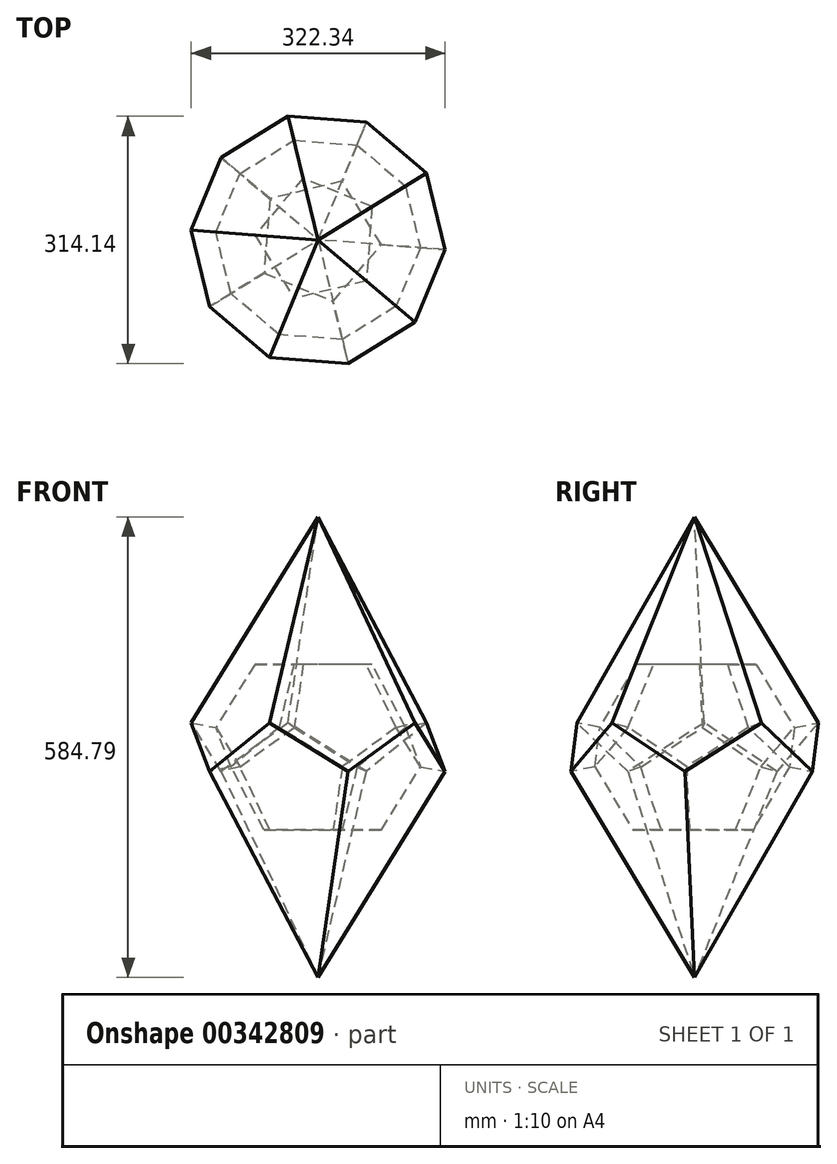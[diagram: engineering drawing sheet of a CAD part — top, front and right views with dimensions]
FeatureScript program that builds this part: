
annotation { "Feature Type Name" : "Feature", "Feature Type Description" : "" }
export const myFeature = defineFeature(function(context is Context, id is Id, definition is map)
    precondition{}
    {
        {
            var Q0;
            Q0=qCreatedBy(makeId("Top.planeOp"),FACE);
            var sketch = newSketch(context, id + "F0", { "sketchPlane" : qUnion([Q0])});
            skCircle(sketch, "E0.cCircle", {"center": v(0, 0) * mm, "radius": 80.82 * mm, "construction": true});
            skLineSegment(sketch, "E0.0", {"start": v(99.6, -7.58) * mm, "end": v(23.57, -97.07) * mm});
            skLineSegment(sketch, "E0.1", {"start": v(23.57, -97.07) * mm, "end": v(-85.04, -52.42) * mm});
            skLineSegment(sketch, "E0.2", {"start": v(-85.04, -52.42) * mm, "end": v(-76.13, 64.68) * mm});
            skLineSegment(sketch, "E0.3", {"start": v(-76.13, 64.68) * mm, "end": v(37.99, 92.39) * mm});
            skLineSegment(sketch, "E0.4", {"start": v(37.99, 92.39) * mm, "end": v(99.6, -7.58) * mm});
            skPoint(sketch, "E0.0.midPoint", {"position": v(61.59, -52.33) * mm});
            skSolve(sketch);
        }
        {
            var Q0;
            Q0=makeQuery(id+"F0.imprint","IMPRINT",FACE,{"disambiguationData":[TD([[makeQuery(id+"F0.imprint","IMPRINT",EDGE,{"derivedFrom":sQuery(id+"F0.wireOp",EDGE,"E0.0")}),-1.0]])]});
            extrude(context, id + "F1", {"entities" : qUnion([Q0]), "depth" : 25.4 * mm});
        }
        {
            var Q0;
            Q0=makeQuery(id+"F1.opExtrude","CAP_EDGE",EDGE,{"disambiguationData":[OSD([sQuery(id+"F0.wireOp",EDGE,"E0.1")])],"isStart":false});
            var Q1;
            Q1=makeQuery(id+"F1.opExtrude","CAP_EDGE",EDGE,{"disambiguationData":[OSD([sQuery(id+"F0.wireOp",EDGE,"E0.2")])],"isStart":false});
            var Q2;
            Q2=makeQuery(id+"F1.opExtrude","CAP_EDGE",EDGE,{"disambiguationData":[OSD([sQuery(id+"F0.wireOp",EDGE,"E0.3")])],"isStart":false});
            var Q3;
            Q3=makeQuery(id+"F1.opExtrude","CAP_EDGE",EDGE,{"disambiguationData":[OSD([sQuery(id+"F0.wireOp",EDGE,"E0.4")])],"isStart":false});
            var Q4;
            Q4=makeQuery(id+"F1.opExtrude","CAP_EDGE",EDGE,{"disambiguationData":[OSD([sQuery(id+"F0.wireOp",EDGE,"E0.0")])],"isStart":false});
            chamfer(context, id + "F2", {"entities" : qUnion([Q0, Q1, Q2, Q3, Q4]), "chamferType" : ChamferType.OFFSET_ANGLE, "width" : 25.4 * mm, "oppositeDirection" : false, "angle" : 31.72 * degree, "tangentPropagation" : true});
        }
        {
            var Q0;
            Q0=makeQuery(id+"F1.opExtrude","SWEPT_BODY",BODY,{"disambiguationData":[OSD([sQuery(id+"F0.wireOp",EDGE,"E0.0"),sQuery(id+"F0.wireOp",EDGE,"E0.1"),sQuery(id+"F0.wireOp",EDGE,"E0.2"),sQuery(id+"F0.wireOp",EDGE,"E0.3"),sQuery(id+"F0.wireOp",EDGE,"E0.4")])]});
            var Q1;
            Q1=makeQuery(id+"F2.opChamfer","BLEND_EDGE",EDGE,{"blendedFrom":[makeQuery(id+"F1.opExtrude","CAP_EDGE",EDGE,{"disambiguationData":[OSD([sQuery(id+"F0.wireOp",EDGE,"E0.1")])],"isStart":false}),makeQuery(id+"F1.opExtrude","CAP_EDGE",EDGE,{"disambiguationData":[OSD([sQuery(id+"F0.wireOp",EDGE,"E0.2")])],"isStart":false})],"blendedInto":[]});
            circularPattern(context, id + "F3", {"entities" : qUnion([Q0]), "axis" : qUnion([Q1]), "angle" : 360 * degree, "instanceCount" : 3, "equalSpace" : true});
        }
        {
            var Q0;
            Q0=makeQuery(id+"F1.opExtrude","SWEPT_BODY",BODY,{"disambiguationData":[OSD([sQuery(id+"F0.wireOp",EDGE,"E0.0"),sQuery(id+"F0.wireOp",EDGE,"E0.1"),sQuery(id+"F0.wireOp",EDGE,"E0.2"),sQuery(id+"F0.wireOp",EDGE,"E0.3"),sQuery(id+"F0.wireOp",EDGE,"E0.4")])]});
            var Q1;
            Q1=makeQuery(id+"F3.opPattern","COPY",BODY,{"derivedFrom":makeQuery(id+"F1.opExtrude","SWEPT_BODY",BODY,{"disambiguationData":[OSD([sQuery(id+"F0.wireOp",EDGE,"E0.0"),sQuery(id+"F0.wireOp",EDGE,"E0.1"),sQuery(id+"F0.wireOp",EDGE,"E0.2"),sQuery(id+"F0.wireOp",EDGE,"E0.3"),sQuery(id+"F0.wireOp",EDGE,"E0.4")])]}),"instanceName":"1"});
            var Q2;
            Q2=makeQuery(id+"F3.opPattern","COPY",BODY,{"derivedFrom":makeQuery(id+"F1.opExtrude","SWEPT_BODY",BODY,{"disambiguationData":[OSD([sQuery(id+"F0.wireOp",EDGE,"E0.0"),sQuery(id+"F0.wireOp",EDGE,"E0.1"),sQuery(id+"F0.wireOp",EDGE,"E0.2"),sQuery(id+"F0.wireOp",EDGE,"E0.3"),sQuery(id+"F0.wireOp",EDGE,"E0.4")])]}),"instanceName":"2"});
            var Q3;
            Q3=makeQuery(id+"F2.opChamfer","BLEND_EDGE",EDGE,{"blendedFrom":[makeQuery(id+"F1.opExtrude","CAP_EDGE",EDGE,{"disambiguationData":[OSD([sQuery(id+"F0.wireOp",EDGE,"E0.0")])],"isStart":false}),makeQuery(id+"F1.opExtrude","CAP_EDGE",EDGE,{"disambiguationData":[OSD([sQuery(id+"F0.wireOp",EDGE,"E0.4")])],"isStart":false})],"blendedInto":[]});
            transform(context, id + "F4", {"entities" : qUnion([Q0, Q1, Q2]), "transformType" : TransformType.ROTATION, "transformAxis" : qUnion([Q3]), "angle" : 120 * degree, "makeCopy" : true});
        }
        {
            var Q0;
            Q0=makeQuery(id+"F4.opPattern","COPY",BODY,{"derivedFrom":makeQuery(id+"F3.opPattern","COPY",BODY,{"derivedFrom":makeQuery(id+"F1.opExtrude","SWEPT_BODY",BODY,{"disambiguationData":[OSD([sQuery(id+"F0.wireOp",EDGE,"E0.0"),sQuery(id+"F0.wireOp",EDGE,"E0.1"),sQuery(id+"F0.wireOp",EDGE,"E0.2"),sQuery(id+"F0.wireOp",EDGE,"E0.3"),sQuery(id+"F0.wireOp",EDGE,"E0.4")])]}),"instanceName":"1"}),"instanceName":"1"});
            var Q1;
            Q1=makeQuery(id+"F4.opPattern","COPY",BODY,{"derivedFrom":makeQuery(id+"F3.opPattern","COPY",BODY,{"derivedFrom":makeQuery(id+"F1.opExtrude","SWEPT_BODY",BODY,{"disambiguationData":[OSD([sQuery(id+"F0.wireOp",EDGE,"E0.0"),sQuery(id+"F0.wireOp",EDGE,"E0.1"),sQuery(id+"F0.wireOp",EDGE,"E0.2"),sQuery(id+"F0.wireOp",EDGE,"E0.3"),sQuery(id+"F0.wireOp",EDGE,"E0.4")])]}),"instanceName":"2"}),"instanceName":"1"});
            var Q2;
            Q2=makeQuery(id+"F4.opPattern","COPY",BODY,{"derivedFrom":makeQuery(id+"F1.opExtrude","SWEPT_BODY",BODY,{"disambiguationData":[OSD([sQuery(id+"F0.wireOp",EDGE,"E0.0"),sQuery(id+"F0.wireOp",EDGE,"E0.1"),sQuery(id+"F0.wireOp",EDGE,"E0.2"),sQuery(id+"F0.wireOp",EDGE,"E0.3"),sQuery(id+"F0.wireOp",EDGE,"E0.4")])]}),"instanceName":"1"});
            var Q3;
            Q3=makeQuery(id+"F4.opPattern","COPY",EDGE,{"derivedFrom":makeQuery(id+"F3.opPattern","COPY",EDGE,{"derivedFrom":makeQuery(id+"F2.opChamfer","BLEND_EDGE",EDGE,{"blendedFrom":[makeQuery(id+"F1.opExtrude","CAP_EDGE",EDGE,{"disambiguationData":[OSD([sQuery(id+"F0.wireOp",EDGE,"E0.0")])],"isStart":false}),makeQuery(id+"F1.opExtrude","CAP_EDGE",EDGE,{"disambiguationData":[OSD([sQuery(id+"F0.wireOp",EDGE,"E0.4")])],"isStart":false})],"blendedInto":[]}),"instanceName":"2"}),"instanceName":"1"});
            transform(context, id + "F5", {"entities" : qUnion([Q0, Q1, Q2]), "transformType" : TransformType.ROTATION, "transformAxis" : qUnion([Q3]), "angle" : 120 * degree, "makeCopy" : true});
        }
        {
            var Q0;
            Q0=makeQuery(id+"F5.opPattern","COPY",BODY,{"derivedFrom":makeQuery(id+"F4.opPattern","COPY",BODY,{"derivedFrom":makeQuery(id+"F1.opExtrude","SWEPT_BODY",BODY,{"disambiguationData":[OSD([sQuery(id+"F0.wireOp",EDGE,"E0.0"),sQuery(id+"F0.wireOp",EDGE,"E0.1"),sQuery(id+"F0.wireOp",EDGE,"E0.2"),sQuery(id+"F0.wireOp",EDGE,"E0.3"),sQuery(id+"F0.wireOp",EDGE,"E0.4")])]}),"instanceName":"1"}),"instanceName":"1"});
            var Q1;
            Q1=makeQuery(id+"F4.opPattern","COPY",BODY,{"derivedFrom":makeQuery(id+"F3.opPattern","COPY",BODY,{"derivedFrom":makeQuery(id+"F1.opExtrude","SWEPT_BODY",BODY,{"disambiguationData":[OSD([sQuery(id+"F0.wireOp",EDGE,"E0.0"),sQuery(id+"F0.wireOp",EDGE,"E0.1"),sQuery(id+"F0.wireOp",EDGE,"E0.2"),sQuery(id+"F0.wireOp",EDGE,"E0.3"),sQuery(id+"F0.wireOp",EDGE,"E0.4")])]}),"instanceName":"2"}),"instanceName":"1"});
            var Q2;
            Q2=makeQuery(id+"F5.opPattern","COPY",BODY,{"derivedFrom":makeQuery(id+"F4.opPattern","COPY",BODY,{"derivedFrom":makeQuery(id+"F3.opPattern","COPY",BODY,{"derivedFrom":makeQuery(id+"F1.opExtrude","SWEPT_BODY",BODY,{"disambiguationData":[OSD([sQuery(id+"F0.wireOp",EDGE,"E0.0"),sQuery(id+"F0.wireOp",EDGE,"E0.1"),sQuery(id+"F0.wireOp",EDGE,"E0.2"),sQuery(id+"F0.wireOp",EDGE,"E0.3"),sQuery(id+"F0.wireOp",EDGE,"E0.4")])]}),"instanceName":"2"}),"instanceName":"1"}),"instanceName":"1"});
            var Q3;
            Q3=makeQuery(id+"F5.opPattern","COPY",EDGE,{"derivedFrom":makeQuery(id+"F4.opPattern","COPY",EDGE,{"derivedFrom":makeQuery(id+"F3.opPattern","COPY",EDGE,{"derivedFrom":makeQuery(id+"F2.opChamfer","BLEND_EDGE",EDGE,{"blendedFrom":[makeQuery(id+"F1.opExtrude","CAP_EDGE",EDGE,{"disambiguationData":[OSD([sQuery(id+"F0.wireOp",EDGE,"E0.2")])],"isStart":false}),makeQuery(id+"F1.opExtrude","CAP_EDGE",EDGE,{"disambiguationData":[OSD([sQuery(id+"F0.wireOp",EDGE,"E0.3")])],"isStart":false})],"blendedInto":[]}),"instanceName":"2"}),"instanceName":"1"}),"instanceName":"1"});
            transform(context, id + "F6", {"entities" : qUnion([Q0, Q1, Q2]), "transformType" : TransformType.ROTATION, "transformAxis" : qUnion([Q3]), "angle" : 240 * degree, "makeCopy" : true});
        }
        {
            var Q0;
            Q0=makeQuery(id+"F6.opPattern","COPY",FACE,{"derivedFrom":makeQuery(id+"F5.opPattern","COPY",FACE,{"derivedFrom":makeQuery(id+"F4.opPattern","COPY",FACE,{"derivedFrom":makeQuery(id+"F3.opPattern","COPY",FACE,{"derivedFrom":makeQuery(id+"F1.opExtrude","CAP_FACE",FACE,{"disambiguationData":[OSD([sQuery(id+"F0.wireOp",EDGE,"E0.0"),sQuery(id+"F0.wireOp",EDGE,"E0.1"),sQuery(id+"F0.wireOp",EDGE,"E0.2"),sQuery(id+"F0.wireOp",EDGE,"E0.3"),sQuery(id+"F0.wireOp",EDGE,"E0.4")])],"isStart":true}),"instanceName":"2"}),"instanceName":"1"}),"instanceName":"1"}),"instanceName":"1"});
            var sketch = newSketch(context, id + "F7", { "sketchPlane" : qUnion([Q0])});
            skLineSegment(sketch, "E1", {"start": v(-103.74, 75.33) * mm, "end": v(-29.05, 432.82) * mm});
            skSolve(sketch);
        }
        {
            var Q0;
            Q0=makeQuery(id+"F6.opPattern","COPY",FACE,{"derivedFrom":makeQuery(id+"F5.opPattern","COPY",FACE,{"derivedFrom":makeQuery(id+"F4.opPattern","COPY",FACE,{"derivedFrom":makeQuery(id+"F1.opExtrude","CAP_FACE",FACE,{"disambiguationData":[OSD([sQuery(id+"F0.wireOp",EDGE,"E0.0"),sQuery(id+"F0.wireOp",EDGE,"E0.1"),sQuery(id+"F0.wireOp",EDGE,"E0.2"),sQuery(id+"F0.wireOp",EDGE,"E0.3"),sQuery(id+"F0.wireOp",EDGE,"E0.4")])],"isStart":true}),"instanceName":"1"}),"instanceName":"1"}),"instanceName":"1"});
            var sketch = newSketch(context, id + "F8", { "sketchPlane" : qUnion([Q0])});
            skLineSegment(sketch, "E2", {"start": v(97.88, 82.8) * mm, "end": v(-27.14, 517.31) * mm});
            skSolve(sketch);
        }
        {
            var Q0;
            {var subQ0=sQuery(id+"F0.wireOp",EDGE,"E0.4");var subQ1=sQuery(id+"F0.wireOp",EDGE,"E0.2");var subQ2=sQuery(id+"F0.wireOp",EDGE,"E0.1");var subQ3=sQuery(id+"F0.wireOp",EDGE,"E0.0");var subQ4=makeQuery(id+"F1.opExtrude","CAP_FACE",FACE,{"disambiguationData":[OSD([subQ3,subQ2,subQ1,sQuery(id+"F0.wireOp",EDGE,"E0.3"),subQ0])],"isStart":true});Q0=makeQuery(id+"F7.imprint","IMPRINT",FACE,{"disambiguationData":[TD([[makeQuery(id+"F7.imprint","IMPRINT",EDGE,{"derivedFrom":makeQuery(id+"F6.opPattern","COPY",EDGE,{"derivedFrom":makeQuery(id+"F5.opPattern","COPY",EDGE,{"derivedFrom":makeQuery(id+"F4.opPattern","COPY",EDGE,{"derivedFrom":makeQuery(id+"F3.opPattern","COPY",EDGE,{"derivedFrom":makeQuery(id+"F2.opChamfer","BLEND_EDGE",EDGE,{"blendedFrom":[makeQuery(id+"F1.opExtrude","CAP_EDGE",EDGE,{"disambiguationData":[OSD([subQ3])],"isStart":false}),subQ4],"blendedInto":[subQ4]}),"instanceName":"2"}),"instanceName":"1"}),"instanceName":"1"}),"instanceName":"1"})}),1.0]])]});}
            var sketch = newSketch(context, id + "F9", { "sketchPlane" : qUnion([Q0])});
            skLineSegment(sketch, "E3", {"start": v(-40.86, 376.27) * mm, "end": v(-0.97, 360.76) * mm});
            skSolve(sketch);
        }
        {
            var Q1;
            Q1=makeQuery(id+"F5.opPattern","COPY",FACE,{"derivedFrom":makeQuery(id+"F4.opPattern","COPY",FACE,{"derivedFrom":makeQuery(id+"F3.opPattern","COPY",FACE,{"derivedFrom":makeQuery(id+"F1.opExtrude","CAP_FACE",FACE,{"disambiguationData":[OSD([sQuery(id+"F0.wireOp",EDGE,"E0.0"),sQuery(id+"F0.wireOp",EDGE,"E0.1"),sQuery(id+"F0.wireOp",EDGE,"E0.2"),sQuery(id+"F0.wireOp",EDGE,"E0.3"),sQuery(id+"F0.wireOp",EDGE,"E0.4")])],"isStart":true}),"instanceName":"2"}),"instanceName":"1"}),"instanceName":"1"});
            var Q2;
            Q2=sQuery(id+"F9.wireOp",VERTEX,"E3.start");
            loft(context, id + "F10", {"operationType" : NewBodyOperationType.ADD, "sheetProfilesArray" : [{ "sheetProfileEntities" : qUnion([Q1]) }, { "sheetProfileEntities" : qUnion([Q2]) }]});
        }
        {
            var Q0;
            Q0=makeQuery(id+"F6.opPattern","COPY",FACE,{"derivedFrom":makeQuery(id+"F4.opPattern","COPY",FACE,{"derivedFrom":makeQuery(id+"F3.opPattern","COPY",FACE,{"derivedFrom":makeQuery(id+"F1.opExtrude","CAP_FACE",FACE,{"disambiguationData":[OSD([sQuery(id+"F0.wireOp",EDGE,"E0.0"),sQuery(id+"F0.wireOp",EDGE,"E0.1"),sQuery(id+"F0.wireOp",EDGE,"E0.2"),sQuery(id+"F0.wireOp",EDGE,"E0.3"),sQuery(id+"F0.wireOp",EDGE,"E0.4")])],"isStart":true}),"instanceName":"2"}),"instanceName":"1"}),"instanceName":"1"});
            var sketch = newSketch(context, id + "F11", { "sketchPlane" : qUnion([Q0])});
            skLineSegment(sketch, "E4", {"start": v(38.24, 132.45) * mm, "end": v(57.54, -261.56) * mm});
            skSolve(sketch);
        }
        {
            var Q0;
            Q0=makeQuery(id+"F3.opPattern","COPY",FACE,{"derivedFrom":makeQuery(id+"F1.opExtrude","CAP_FACE",FACE,{"disambiguationData":[OSD([sQuery(id+"F0.wireOp",EDGE,"E0.0"),sQuery(id+"F0.wireOp",EDGE,"E0.1"),sQuery(id+"F0.wireOp",EDGE,"E0.2"),sQuery(id+"F0.wireOp",EDGE,"E0.3"),sQuery(id+"F0.wireOp",EDGE,"E0.4")])],"isStart":true}),"instanceName":"1"});
            var sketch = newSketch(context, id + "F12", { "sketchPlane" : qUnion([Q0])});
            skLineSegment(sketch, "E5", {"start": v(63.3, 137.03) * mm, "end": v(11.57, -251.7) * mm});
            skLineSegment(sketch, "E6", {"start": v(-108.02, 105.75) * mm, "end": v(104.5, -286.97) * mm});
            skLineSegment(sketch, "E7", {"start": v(-9.37, -80.49) * mm, "end": v(26.14, -142.18) * mm});
            skSolve(sketch);
        }
        {
            var Q1;
            Q1=makeQuery(id+"F1.opExtrude","CAP_FACE",FACE,{"disambiguationData":[OSD([sQuery(id+"F0.wireOp",EDGE,"E0.0"),sQuery(id+"F0.wireOp",EDGE,"E0.1"),sQuery(id+"F0.wireOp",EDGE,"E0.2"),sQuery(id+"F0.wireOp",EDGE,"E0.3"),sQuery(id+"F0.wireOp",EDGE,"E0.4")])],"isStart":true});
            var Q2;
            Q2=sQuery(id+"F12.wireOp",VERTEX,"E7.end");
            loft(context, id + "F13", {"operationType" : NewBodyOperationType.ADD, "sheetProfilesArray" : [{ "sheetProfileEntities" : qUnion([Q1]) }, { "sheetProfileEntities" : qUnion([Q2]) }]});
        }
    });
